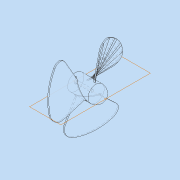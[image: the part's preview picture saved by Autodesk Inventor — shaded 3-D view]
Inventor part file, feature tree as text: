
AUTODESK INVENTOR PART (.ipt)
format: ipt  version: 2015 (Build 190159000, 159)  size: 183,808 bytes
history: native  units: mm
features: fillet x3, sketch x2, extrude x1, helix x1, pattern_circular x1, hole x1
ambient origin geometry x8: Origin, YZ Plane, XZ Plane, XY Plane, X Axis, Y Axis, Z Axis, Center Point
bodies: Solid1 (feature_tree)
feature tree (9):
  extrude  "Extrusion1"  Depth=1.5mm TaperAngle=0.0deg
  fillet  "Fillet1"  Radius=10.0mm
  helix  "Coil1"  [1 undecoded]
  fillet  "Fillet2"  Radius=1.5mm
  fillet  "Fillet3"  Radius=5.0mm
  pattern_circular  "Circular Pattern1"  [2 undecoded]
  hole  "Hole1"  [1 undecoded]
  sketch  "Sketch1"  dims[d0=20.0mm d1=35.0mm d2=0.0mm d3=10.0mm d6=40.0mm d7=1.5mm d8=5.0mm]
  sketch  "Sketch3"  dims[d9=70.0mm d10=15.0mm d11=10.0mm d12=0.0mm d13=90.0deg d14=90.0deg d15=0.0mm d16=0.0mm d17=10.0mm d18=2.0mm d19=30.0mm d20=360.0deg d33=10.0mm d34=10.0mm d24=3.0mm d25=6.0mm d26=5.0mm d27=2.0mm d28=90.0deg d29=20.0mm d30=20.594885mm]
note: 4 required parameter values undecoded (feature->parameter linkage not recoverable at this tier; creation-order binding heuristic only, values carry confidence <= 0.55)
